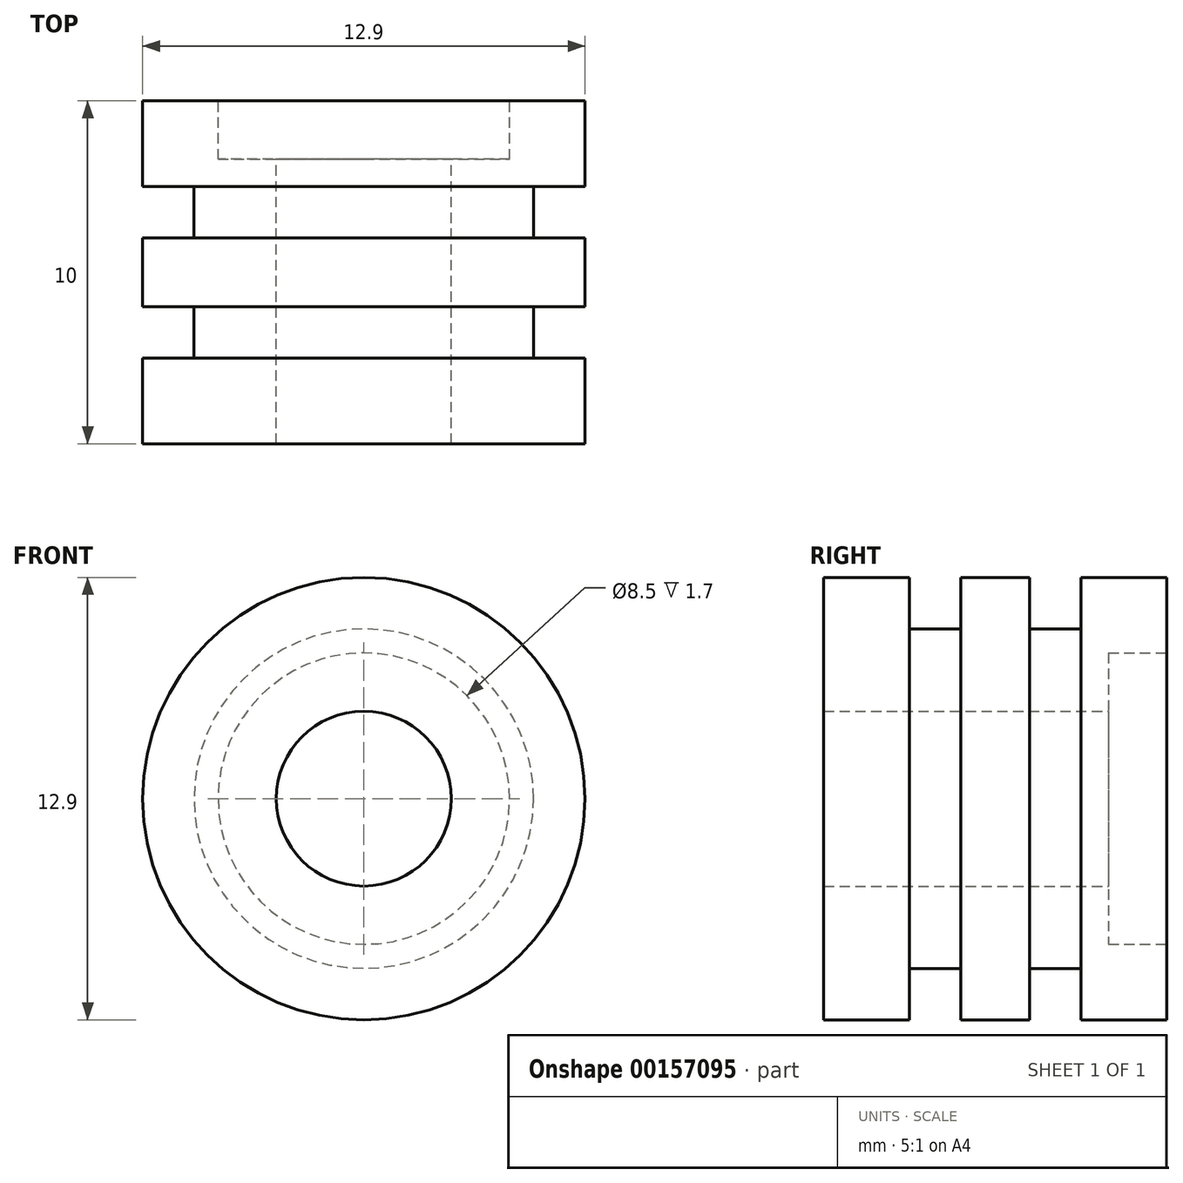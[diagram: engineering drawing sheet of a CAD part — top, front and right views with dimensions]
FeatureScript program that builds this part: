
annotation { "Feature Type Name" : "Feature", "Feature Type Description" : "" }
export const myFeature = defineFeature(function(context is Context, id is Id, definition is map)
    precondition{}
    {
        {
            var Q0;
            Q0=qCreatedBy(makeId("Right.planeOp"),FACE);
            var sketch = newSketch(context, id + "F0", { "sketchPlane" : qUnion([Q0])});
            skLineSegment(sketch, "E0", {"start": v(11.47, 0) * mm, "end": v(0, 0) * mm, "construction": true});
            skLineSegment(sketch, "E1", {"start": v(8.3, 2.55) * mm, "end": v(0, 2.55) * mm});
            skLineSegment(sketch, "E2", {"start": v(8.3, 2.55) * mm, "end": v(8.3, 4.25) * mm});
            skLineSegment(sketch, "E3", {"start": v(10, 4.25) * mm, "end": v(8.3, 4.25) * mm});
            skLineSegment(sketch, "E4", {"start": v(10, 4.25) * mm, "end": v(10, 6.45) * mm});
            skLineSegment(sketch, "E5", {"start": v(7.5, 6.45) * mm, "end": v(10, 6.45) * mm});
            skLineSegment(sketch, "E6", {"start": v(7.5, 6.45) * mm, "end": v(7.5, 4.95) * mm});
            skLineSegment(sketch, "E7", {"start": v(6, 4.95) * mm, "end": v(7.5, 4.95) * mm});
            skLineSegment(sketch, "E8", {"start": v(2.5, 4.95) * mm, "end": v(2.5, 6.45) * mm});
            skLineSegment(sketch, "E9", {"start": v(0, 6.45) * mm, "end": v(2.5, 6.45) * mm});
            skLineSegment(sketch, "E10", {"start": v(0, 6.45) * mm, "end": v(0, 2.55) * mm});
            skLineSegment(sketch, "E11", {"start": v(4, 4.95) * mm, "end": v(4, 6.45) * mm});
            skLineSegment(sketch, "E12", {"start": v(4, 6.45) * mm, "end": v(6, 6.45) * mm});
            skLineSegment(sketch, "E13", {"start": v(6, 6.45) * mm, "end": v(6, 4.95) * mm});
            skLineSegment(sketch, "E14.trimOffspring", {"start": v(4, 4.95) * mm, "end": v(2.5, 4.95) * mm});
            skSolve(sketch);
        }
        {
            var Q0;
            Q0=makeQuery(id+"F0.imprint","IMPRINT",FACE,{"disambiguationData":[TD([[makeQuery(id+"F0.imprint","IMPRINT",EDGE,{"derivedFrom":sQuery(id+"F0.wireOp",EDGE,"E1")}),-1.0]])]});
            var Q1;
            Q1=sQuery(id+"F0.wireOp",EDGE,"E0");
            revolve(context, id + "F1", {"entities" : qUnion([Q0]), "axis" : qUnion([Q1]), "revolveType" : RevolveType.FULL});
        }
    });
